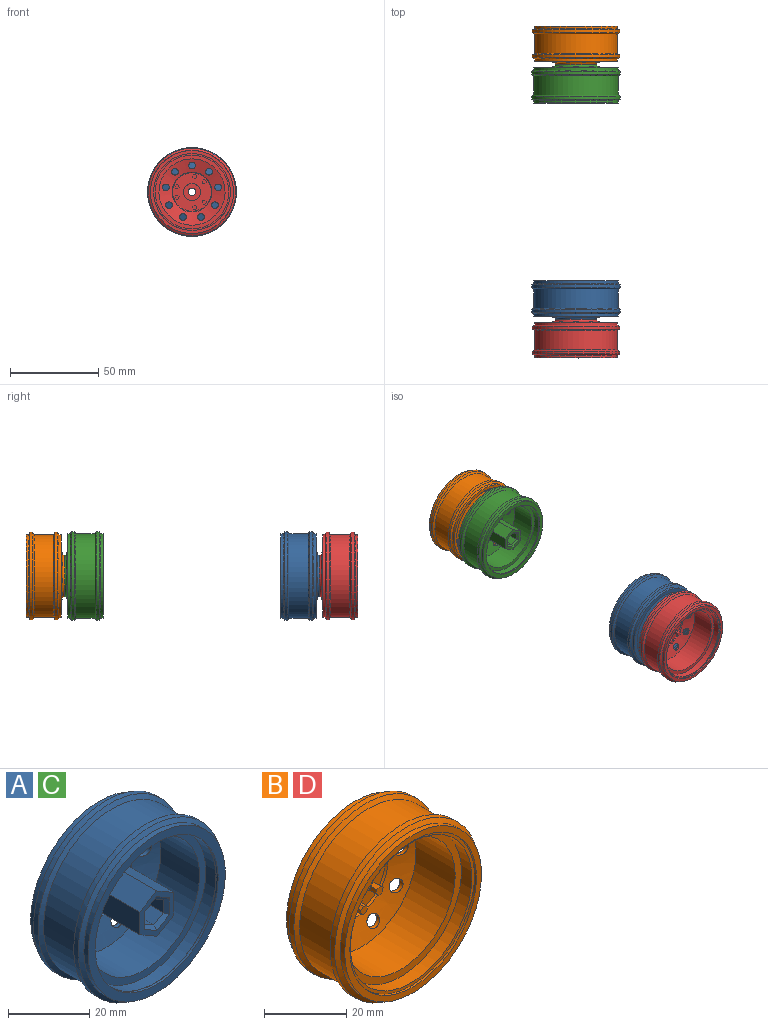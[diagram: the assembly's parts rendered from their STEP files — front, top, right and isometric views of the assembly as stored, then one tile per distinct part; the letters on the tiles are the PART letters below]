
ASSEMBLY  parts=4 mates=6
PART A: 57 faces, bbox 50.3x21.8x50.3 mm
  f0: cone r=21.41mm half-angle=89.1deg, axis (0,-1,0), area 7.1mm2, adj f17,f50
  f1: plane 42.82x42.82mm, normal (0,-1,0), area 11.6mm2, adj f18,f38
  f2: cylinder r=1.9mm len=3.8mm, axis (0,-1,0), area 13.8mm2, adj f14,f21
  f3: cylinder r=1.9mm len=3.8mm, axis (0,-1,0), area 13.8mm2, adj f14,f21
  f4: cylinder r=1.9mm len=3.8mm, axis (0,-1,0), area 13.8mm2, adj f14,f21
  f5: cylinder r=1.9mm len=3.8mm, axis (0,-1,0), area 13.8mm2, adj f14,f21
  f6: cylinder r=1.9mm len=3.8mm, axis (0,-1,0), area 13.8mm2, adj f14,f21
  f7: cylinder r=1.9mm len=3.8mm, axis (0,-1,0), area 13.8mm2, adj f14,f21
  f8: cylinder r=1.9mm len=3.8mm, axis (0,-1,0), area 13.8mm2, adj f14,f21
  f9: cylinder r=1.9mm len=3.8mm, axis (0,-1,0), area 13.8mm2, adj f14,f21
  f10: plane 21.81x21.81mm, normal (0,-1,0), area 252.3mm2, adj f22,f25,f26,f27,f28,f29,f36
  f11: cylinder r=2.12mm len=4.25mm, axis (0,1,0), area 18.5mm2, adj f12,f23
  f12: plane 23x23mm, normal (0,1,0), area 401.3mm2, adj f11,f13
  f13: cone r=11.5mm half-angle=26.6deg, axis (0,-1,0), area 82.5mm2, adj f12,f14
  f14: cone r=12mm half-angle=74.8deg, axis (0,-1,0), area 787.9mm2, adj f2,f3,f4,f5,f6,f7,f8,f9
  f15: cone r=20.46mm half-angle=3.1deg, axis (0,-1,0), area 398.5mm2, adj f14,f16
  f16: plane 42.18x42.18mm, normal (0,1,0), area 60.9mm2, adj f15,f17
  f17: cone r=21.09mm half-angle=4.6deg, axis (0,1,0), area 534.4mm2, adj f0,f16
  f18: cylinder r=21.33mm len=42.65mm, axis (0,1,0), area 473mm2, adj f1,f19
  f19: plane 42.65x42.65mm, normal (0,-1,0), area 276.6mm2, adj f18,f20
  f20: cylinder r=19.15mm len=38.3mm, axis (0,1,0), area 1620.7mm2, adj f19,f21
  f21: cone r=19.15mm half-angle=74.7deg, axis (0,-1,0), area 681.5mm2, adj f2,f3,f4,f5,f6,f7,f8,f9
  f22: cone r=11.18mm half-angle=26.8deg, axis (0,-1,0), area 42.1mm2, adj f10,f21
  f23: plane 7.9x6.84mm, normal (0,-1,0), area 26.4mm2, adj f11,f30,f31,f32,f33,f34,f35
  f24: plane 13.67x11.84mm, normal (0,-1,0), area 53.7mm2, adj f25,f26,f27,f28,f29,f36,f51,f52
  f25: plane 20.42x6.84mm, normal (1,0,0), area 139.6mm2, adj f10,f24,f26,f36
  f26: plane 20.42x5.92mm, normal (0.5,0,0.87), area 139.6mm2, adj f10,f24,f25,f27
  f27: plane 20.42x5.92mm, normal (-0.5,0,0.87), area 139.6mm2, adj f10,f24,f26,f28
  f28: plane 20.42x6.84mm, normal (-1,0,0), area 139.6mm2, adj f10,f24,f27,f29
  f29: plane 20.42x5.92mm, normal (-0.5,0,-0.87), area 139.6mm2, adj f10,f24,f28,f36
  f30: plane 19.42x3.42mm, normal (0.5,0,-0.87), area 76.7mm2, adj f23,f31,f35,f51
  f31: plane 19.42x3.42mm, normal (-0.5,0,-0.87), area 76.7mm2, adj f23,f30,f32,f53
  f32: plane 19.42x3.95mm, normal (-1,0,0), area 76.7mm2, adj f23,f31,f33,f55
  f33: plane 19.42x3.42mm, normal (-0.5,0,0.87), area 76.7mm2, adj f23,f32,f34,f56
  f34: plane 19.42x3.42mm, normal (0.5,0,0.87), area 76.7mm2, adj f23,f33,f35,f54
  f35: plane 19.42x3.95mm, normal (1,0,0), area 76.7mm2, adj f23,f30,f34,f52
  f36: plane 20.42x5.92mm, normal (0.5,0,-0.87), area 139.6mm2, adj f10,f24,f25,f29
  f37: cylinder r=1.9mm len=3.8mm, axis (0,-1,0), area 13.8mm2, adj f14,f21
  f38: cylinder r=21.41mm len=42.82mm, axis (0,-1,0), area 93.1mm2, adj f1,f39
  f39: plane 47.78x47.78mm, normal (0,-1,0), area 352.5mm2, adj f38,f40
  f40: cylinder r=23.89mm len=47.78mm, axis (0,1,0), area 225.1mm2, adj f39,f42
  f41: cylinder r=25.14mm len=50.28mm, axis (0,-1,0), area 245.9mm2, adj f42,f43
  f42: cone r=23.89mm half-angle=60deg, axis (0,1,0), area 222.3mm2, adj f40,f41
  f43: cone r=25.14mm half-angle=60deg, axis (0,-1,0), area 222.3mm2, adj f41,f44
  f44: cylinder r=23.89mm len=47.78mm, axis (0,1,0), area 1653.7mm2, adj f43,f45
  f45: cone r=23.89mm half-angle=60deg, axis (0,1,0), area 222.3mm2, adj f44,f46
  f46: cylinder r=25.14mm len=50.28mm, axis (0,-1,0), area 245.9mm2, adj f45,f47
  f47: cone r=25.14mm half-angle=60deg, axis (0,-1,0), area 222.3mm2, adj f46,f48
  f48: cylinder r=23.89mm len=47.78mm, axis (0,1,0), area 225.1mm2, adj f47,f49
  f49: plane 47.78x47.78mm, normal (0,1,0), area 345.9mm2, adj f48,f50
  f50: cylinder r=21.46mm len=42.92mm, axis (0,-1,0), area 81.6mm2, adj f0,f49
  f51: plane 4.42x3.13mm, normal (0.35,-0.71,-0.61), area 6.4mm2, adj f24,f30,f52,f53
  f52: plane 5.1x1mm, normal (0.71,-0.71,0), area 6.4mm2, adj f24,f35,f51,f54
  f53: plane 4.42x3.13mm, normal (-0.35,-0.71,-0.61), area 6.4mm2, adj f24,f31,f51,f55
  f54: plane 4.42x3.13mm, normal (0.35,-0.71,0.61), area 6.4mm2, adj f24,f34,f52,f56
  f55: plane 5.1x1mm, normal (-0.71,-0.71,0), area 6.4mm2, adj f24,f32,f53,f56
  f56: plane 4.42x3.13mm, normal (-0.35,-0.71,0.61), area 6.4mm2, adj f24,f33,f54,f55
PART B: 81 faces, bbox 49.5x21.8x49.5 mm
  f0: plane 43.39x43.39mm, normal (0,1,0), area 85.4mm2, adj f45,f80
  f1: plane 43.52x43.52mm, normal (0,-1,0), area 118.3mm2, adj f46,f68
  f2: cylinder r=1.9mm len=3.8mm, axis (0,1,0), area 12.5mm2, adj f10,f11
  f3: cylinder r=1.9mm len=3.8mm, axis (0,1,0), area 12.5mm2, adj f10,f11
  f4: cylinder r=1.9mm len=3.8mm, axis (0,1,0), area 12.5mm2, adj f10,f11
  f5: cylinder r=1.9mm len=3.8mm, axis (0,1,0), area 12.5mm2, adj f10,f11
  f6: cylinder r=1.9mm len=3.8mm, axis (0,1,0), area 12.5mm2, adj f10,f11
  f7: cylinder r=1.9mm len=3.8mm, axis (0,1,0), area 12.5mm2, adj f10,f11
  f8: cylinder r=1.9mm len=3.8mm, axis (0,1,0), area 12.5mm2, adj f10,f11
  f9: cylinder r=1.9mm len=3.8mm, axis (0,1,0), area 12.5mm2, adj f10,f11
  f10: cone r=19.96mm half-angle=73.8deg, axis (0,-1,0), area 725.6mm2, adj f2,f3,f4,f5,f6,f7,f8,f9
  f11: cone r=11.3mm half-angle=73.1deg, axis (0,-1,0), area 626.9mm2, adj f2,f3,f4,f5,f6,f7,f8,f9
  f12: plane 2.12x1.25mm, normal (-0.98,0,0.17), area 2.7mm2, adj f13,f17,f18,f50
  f13: plane 2.12x0.97mm, normal (-0.64,0,-0.77), area 2.7mm2, adj f12,f14,f18,f50
  f14: plane 2.12x1.19mm, normal (0.34,0,-0.94), area 2.7mm2, adj f13,f15,f18,f50
  f15: plane 2.12x1.25mm, normal (0.98,0,-0.17), area 2.7mm2, adj f14,f16,f18,f50
  f16: plane 2.12x0.97mm, normal (0.64,0,0.77), area 2.7mm2, adj f15,f17,f18,f50
  f17: plane 2.12x1.19mm, normal (-0.34,0,0.94), area 2.7mm2, adj f12,f16,f18,f50
  f18: plane 2.5x2.39mm, normal (0,-1,0), area 4.2mm2, adj f12,f13,f14,f15,f16,f17
  f19: plane 2.12x0.97mm, normal (-0.64,0,0.77), area 2.7mm2, adj f20,f24,f25,f50
  f20: plane 2.12x1.25mm, normal (-0.98,0,-0.17), area 2.7mm2, adj f19,f21,f25,f50
  f21: plane 2.12x1.19mm, normal (-0.34,0,-0.94), area 2.7mm2, adj f20,f22,f25,f50
  f22: plane 2.12x0.97mm, normal (0.64,0,-0.77), area 2.7mm2, adj f21,f23,f25,f50
  f23: plane 2.12x1.25mm, normal (0.98,0,0.17), area 2.7mm2, adj f22,f24,f25,f50
  f24: plane 2.12x1.19mm, normal (0.34,0,0.94), area 2.7mm2, adj f19,f23,f25,f50
  f25: plane 2.5x2.39mm, normal (0,-1,0), area 4.2mm2, adj f19,f20,f21,f22,f23,f24
  f26: plane 2.12x1.19mm, normal (0.34,0,-0.94), area 2.7mm2, adj f27,f31,f32,f50
  f27: plane 2.12x1.25mm, normal (0.98,0,-0.17), area 2.7mm2, adj f26,f28,f32,f50
  f28: plane 2.12x0.97mm, normal (0.64,0,0.77), area 2.7mm2, adj f27,f29,f32,f50
  f29: plane 2.12x1.19mm, normal (-0.34,0,0.94), area 2.7mm2, adj f28,f30,f32,f50
  f30: plane 2.12x1.25mm, normal (-0.98,0,0.17), area 2.7mm2, adj f29,f31,f32,f50
  f31: plane 2.12x0.97mm, normal (-0.64,0,-0.77), area 2.7mm2, adj f26,f30,f32,f50
  f32: plane 2.5x2.39mm, normal (0,-1,0), area 4.2mm2, adj f26,f27,f28,f29,f30,f31
  f33: plane 2.12x1.19mm, normal (-0.34,0,-0.94), area 2.7mm2, adj f34,f38,f39,f50
  f34: plane 2.12x0.97mm, normal (0.64,0,-0.77), area 2.7mm2, adj f33,f35,f39,f50
  f35: plane 2.12x1.25mm, normal (0.98,0,0.17), area 2.7mm2, adj f34,f36,f39,f50
  f36: plane 2.12x1.19mm, normal (0.34,0,0.94), area 2.7mm2, adj f35,f37,f39,f50
  f37: plane 2.12x0.97mm, normal (-0.64,0,0.77), area 2.7mm2, adj f36,f38,f39,f50
  f38: plane 2.12x1.25mm, normal (-0.98,0,-0.17), area 2.7mm2, adj f33,f37,f39,f50
  f39: plane 2.5x2.39mm, normal (0,-1,0), area 4.2mm2, adj f33,f34,f35,f36,f37,f38
  f40: cylinder r=2.08mm len=4.16mm, axis (0,1,0), area 44.3mm2, adj f41,f52
  f41: plane 23x23mm, normal (0,1,0), area 401.9mm2, adj f40,f42
  f42: cone r=12mm half-angle=26.6deg, axis (0,-1,0), area 82.5mm2, adj f10,f41
  f43: cone r=20.19mm half-angle=4.4deg, axis (0,-1,0), area 387.8mm2, adj f10,f44
  f44: plane 41.29x41.29mm, normal (0,1,0), area 57.9mm2, adj f43,f45
  f45: cone r=21.06mm half-angle=5.9deg, axis (0,1,0), area 527.5mm2, adj f0,f44
  f46: cylinder r=20.88mm len=41.75mm, axis (0,1,0), area 473.3mm2, adj f1,f47
  f47: plane 41.75x41.75mm, normal (0,-1,0), area 266.4mm2, adj f46,f48
  f48: cylinder r=18.73mm len=37.47mm, axis (0,1,0), area 1584.5mm2, adj f11,f47
  f49: cone r=10.92mm half-angle=35.1deg, axis (0,-1,0), area 45.7mm2, adj f11,f50
  f50: plane 21.85x21.85mm, normal (0,-1,0), area 276.2mm2, adj f12,f13,f14,f15,f16,f17,f19,f20
  f51: cylinder r=4.84mm len=9.68mm, axis (0,1,0), area 64.5mm2, adj f50,f52
  f52: plane 9.68x9.68mm, normal (0,-1,0), area 59.9mm2, adj f40,f51
  f53: plane 2.12x1.19mm, normal (0.34,0,0.94), area 2.7mm2, adj f50,f54,f56,f57
  f54: plane 2.12x0.97mm, normal (-0.64,0,0.77), area 2.7mm2, adj f50,f53,f55,f56
  f55: plane 2.12x1.25mm, normal (-0.98,0,-0.17), area 2.7mm2, adj f50,f54,f56,f58
  f56: plane 2.5x2.39mm, normal (0,-1,0), area 4.2mm2, adj f53,f54,f55,f57,f58,f59
  f57: plane 2.12x1.25mm, normal (0.98,0,0.17), area 2.7mm2, adj f50,f53,f56,f59
  f58: plane 2.12x1.19mm, normal (-0.34,0,-0.94), area 2.7mm2, adj f50,f55,f56,f59
  f59: plane 2.12x0.97mm, normal (0.64,0,-0.77), area 2.7mm2, adj f50,f56,f57,f58
  f60: plane 2.12x1.19mm, normal (-0.34,0,0.94), area 2.7mm2, adj f50,f61,f63,f64
  f61: plane 2.12x1.25mm, normal (-0.98,0,0.17), area 2.7mm2, adj f50,f60,f62,f63
  f62: plane 2.12x0.97mm, normal (-0.64,0,-0.77), area 2.7mm2, adj f50,f61,f63,f65
  f63: plane 2.5x2.39mm, normal (0,-1,0), area 4.2mm2, adj f60,f61,f62,f64,f65,f66
  f64: plane 2.12x0.97mm, normal (0.64,0,0.77), area 2.7mm2, adj f50,f60,f63,f66
  f65: plane 2.12x1.19mm, normal (0.34,0,-0.94), area 2.7mm2, adj f50,f62,f63,f66
  f66: plane 2.12x1.25mm, normal (0.98,0,-0.17), area 2.7mm2, adj f50,f63,f64,f65
  f67: cylinder r=1.9mm len=3.8mm, axis (0,1,0), area 12.5mm2, adj f10,f11
  f68: cylinder r=21.76mm len=43.52mm, axis (0,-1,0), area 92.2mm2, adj f1,f69
  f69: plane 47.03x47.03mm, normal (0,-1,0), area 249.4mm2, adj f68,f70
  f70: cylinder r=23.51mm len=47.03mm, axis (0,1,0), area 221.6mm2, adj f69,f72
  f71: cylinder r=24.76mm len=49.53mm, axis (0,-1,0), area 242.2mm2, adj f72,f73
  f72: cone r=23.51mm half-angle=60deg, axis (0,1,0), area 218.9mm2, adj f70,f71
  f73: cone r=24.76mm half-angle=60deg, axis (0,-1,0), area 218.9mm2, adj f71,f74
  f74: cylinder r=23.51mm len=47.03mm, axis (0,1,0), area 1630.4mm2, adj f73,f75
  f75: cone r=23.51mm half-angle=60deg, axis (0,1,0), area 218.9mm2, adj f74,f76
  f76: cylinder r=24.76mm len=49.53mm, axis (0,-1,0), area 242.2mm2, adj f75,f77
  f77: cone r=24.76mm half-angle=60deg, axis (0,-1,0), area 218.9mm2, adj f76,f78
  f78: cylinder r=23.51mm len=47.03mm, axis (0,1,0), area 221.6mm2, adj f77,f79
  f79: plane 47.03x47.03mm, normal (0,1,0), area 257.8mm2, adj f78,f80
  f80: cylinder r=21.7mm len=43.39mm, axis (0,-1,0), area 83.8mm2, adj f0,f79
PART C: same geometry as A
PART D: same geometry as B
PLACE A rot(axis=(1,0,0),180deg) t=(79.65,50.3,-35.07)mm
PLACE B rot(axis=(1,0,0),180deg) t=(79.65,172.9,-35.07)mm
PLACE C t=(79.65,151.1,-35.07)mm
PLACE D t=(79.65,28.5,-35.07)mm
MATE planar C.f0 <-> B.f10  axis (0,1,0) through (79.65,172.9,-35.07)mm
MATE planar D.f10 <-> A.f0  axis (0,1,0) through (79.65,28.5,-35.07)mm
MATE cylindrical B.f10 <-> C.f0  axis (0,-1,0) through (79.65,174.59,-35.07)mm
MATE cylindrical A.f0 <-> D.f10  axis (0,-1,0) through (79.65,29.19,-35.07)mm
MATE cylindrical B.f10 <-> D.f10  axis (0,-1,0) through (79.65,174.59,-35.07)mm
MATE planar B.f10 <-> D.f10  axis (0,1,0) through (79.65,194.7,-35.07)mm
